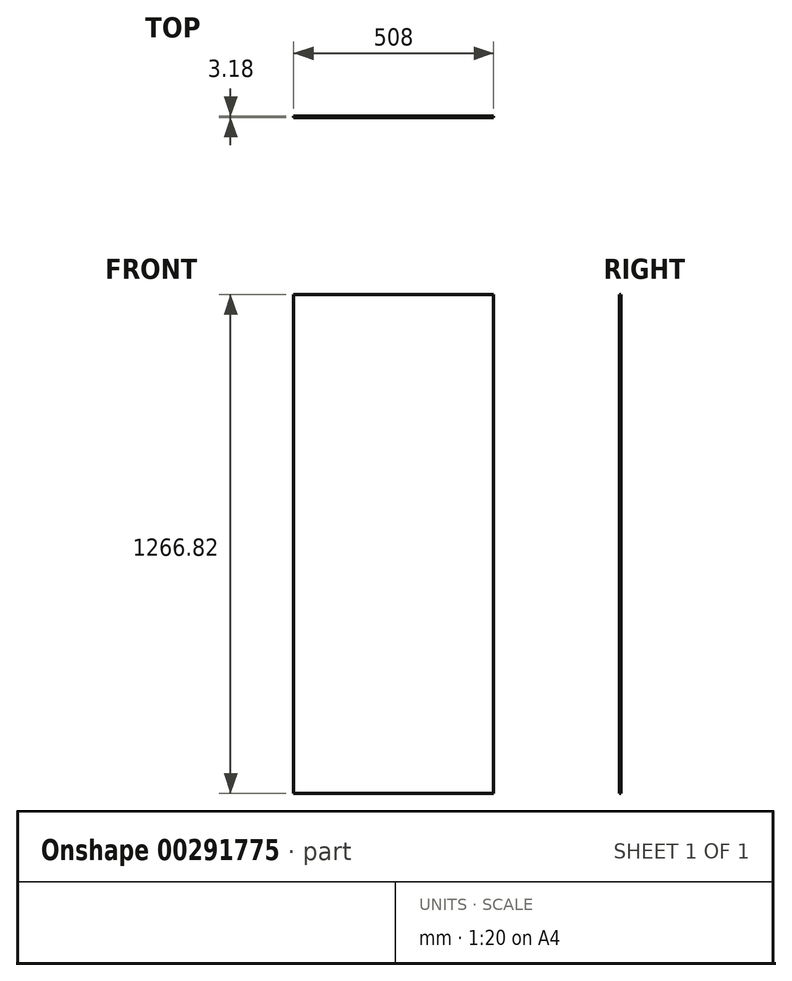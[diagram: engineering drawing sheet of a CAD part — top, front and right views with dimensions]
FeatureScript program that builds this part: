
annotation { "Feature Type Name" : "Feature", "Feature Type Description" : "" }
export const myFeature = defineFeature(function(context is Context, id is Id, definition is map)
    precondition{}
    {
        {
            var Q0;
            Q0=qCreatedBy(makeId("Front.planeOp"),FACE);
            var sketch = newSketch(context, id + "F0", { "sketchPlane" : qUnion([Q0])});
            skLineSegment(sketch, "E0.bottom", {"start": v(254, 633.41) * mm, "end": v(-254, 633.41) * mm});
            skLineSegment(sketch, "E0.top", {"start": v(254, -633.41) * mm, "end": v(-254, -633.41) * mm});
            skLineSegment(sketch, "E0.left", {"start": v(254, 633.41) * mm, "end": v(254, -633.41) * mm});
            skLineSegment(sketch, "E0.right", {"start": v(-254, 633.41) * mm, "end": v(-254, -633.41) * mm});
            skPoint(sketch, "E0.middle", {"position": v(0, 0) * mm});
            skSolve(sketch);
        }
        {
            var Q0;
            Q0 = qSketchRegion(id + "F0", true);
            extrude(context, id + "F1", {"entities" : qUnion([Q0]), "endBound" : BoundingType.SYMMETRIC, "depth" : 3.17 * mm});
        }
    });
